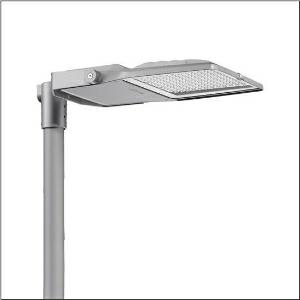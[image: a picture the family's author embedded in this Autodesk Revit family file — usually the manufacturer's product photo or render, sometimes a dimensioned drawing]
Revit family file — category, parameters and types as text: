
# Revit family: floodlight_fl_21_midi___pl52_5xa7786e4d3a_a426
name_source: partatom
category: Lighting Fixtures
units: mm (PartAtom-declared; Revit-internal decimal feet)

## family parameters
Cut with Voids When Loaded = No
Host = Face
Light Source = No
Part Type = Normal
Room Calculation Point = No
Round Connector Dimension = Use Diameter
Shared = No

## types (1)
- --- (1 x LED, 28110 lm, 212.4 W, 4000K)
    Apparent Load = 212 VA
    CIE Flux Codes = 26 60 98 100 100
    Color Rendering = 70
    Color Temperature = 4000K
    Default Elevation = 1800 mm
    Description = Floodlight FL 21 midi, floodlight, primary light control with lens, of PMMA, primary optical cover: protective disc, of toughened safety glass, transparent, light distribution: PL52, light emission: direct distribution, installation type: surface-mounted, LED, High Power LED, rated luminous flux: 28.110lm, luminous efficacy: 132lm/W, light colour: 740, colour temperature: 4000K, control gear: Smart Interface (Zhaga)D4i, control: overheat protection, constant luminous flux control, time-dependent luminous flux control, flexible luminous flux parameterisation, pre-setting: logarithmic dimming characteristic, with terminal, 6-pole, mains connection: 220..240V, AC, 50/60Hz, start of lifetime: 212W, end of service life: 231W, reduction: 95W, mast bracket, of diecast aluminium, powder-coated, SITECO metallic grey (DB 702S), corrosivity category C5 mid according to DIN EN ISO 12944, suitable for swimming pools, chlorine-resistant, sealing non-destructively replaceable, mast bracket, of steel, galvanised, powder-coated, SITECO metallic grey (DB 702S), Smart Interface below and above, protection rating (complete): IP66, insulation class (complete): insulation class II (safety insulation), certification: CE, ENEC, VDE, protection symbol: D, impact resistance: IK08, permissible operating ambient temperature: -40..+40°C, permissible operating ambient temperature for outdoor applications: -40..+50°C, standard: DIN EN 12944, LABS conformity tested according to VDMA 24364:2018-05, packaging unit: 1 piece

Light Distribution: PL52
    Height = 76 mm
    Lamp = 1 x LED
    Lamp Light Flux = 28110 lm
    Lamp Power = 212.4 W
    Lamp count = 1
    Length = 657 mm
    Luminous efficacy = 132 lm/W
    Manufacturer = Siteco
    ModVariant = No
    Model = 5XA7786E4D3A
    Number of Poles = 1
    OnlyDefault = Yes
    Power Factor = 1
    Product Name = Floodlight FL 21 midi | PL52
    Product group = floodlight | pylon annexe
    ProductGroupID = 6201
    Protection Class = Protection class II
    Protection Degree = IP 66
    RLX_Detail_Level = 1
    RLX_Emergency_Light_Flux = 0 lm
    RLX_Emergency_Type = 0
    RLX_Emergency_Type_DB = No
    RlxData = <blob elided: 104833 chars, md5=ce6a9dc0>
    Socket = socket
    Standby Power = 0 W
    System Light Flux = 28110 lm
    System Power = 212 W
    Type Comments = factory setting: luminous flux: 100 % | dim-lin: 254 | 710 mA
    Type Image = l_1007123.jpg
    URL = http://relux.com
    VarID = @adj_093145
    Voltage = 0 V
    Weight = 0.00 kg
    Width = 442 mm

## geometry (parser evidence)
native form markers: Blend x4, Sweep x11
no freeform markers — native parametric forms only
